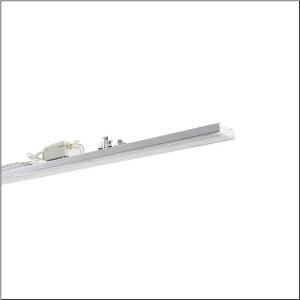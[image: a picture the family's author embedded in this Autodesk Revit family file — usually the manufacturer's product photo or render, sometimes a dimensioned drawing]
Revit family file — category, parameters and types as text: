
# Revit family: licross_r__21_recessed_ho_52te12dv4l2m3s4_36cd
name_source: partatom
category: Lighting Fixtures
units: mm (PartAtom-declared; Revit-internal decimal feet)

## family parameters
Cut with Voids When Loaded = No
Host = Face
Light Source = No
Part Type = Normal
Room Calculation Point = No
Round Connector Dimension = Use Diameter
Shared = No

## types (1)
- --- (1 x LED, 910 lm, 6.4 W, 4000K)
    Apparent Load = 6 VA
    CIE Flux Codes = 69 91 98 100 100
    Color Rendering = 80
    Color Temperature = 4000K
    Default Elevation = 1800 mm
    Description = Licross® 21 Recessed HO, luminaire insert, of sheet steel, galvanised, coil coated, white, length: 2.250mm, width: 66mm, height: 67mm, LED rated luminous flux: 22.710lm, light colour: 840, control gear: DALI 2, with plug, 6-pole, with phase selection, for trunking rail, 9 or 11-core, mains connection: 220..240V, AC, 50/60Hz, rated input power: 129W, for trunking rail, 9-/11-core, halogen-free wiring, for emergency light function, converter,control gear: single battery element, battery: LiFeP04, 9Ah, primary optical cover: cover, of PMMA, light emission: direct distribution, primary light characteristic: symmetric, protection rating (complete): IP54, insulation class (complete): insulation class I (protective earthing), certification: CE, UKCA, protection symbol: D if used in an environment with non-conductive dust loads with corresponding accessories, impact resistance: IK06, permissible ambient temperature for indoor applications: +5..+30°C, standard: EN 60598-2-22, LABS conformity tested according to VDMA 24364:2018-05, reducing of maximum allowable ambient temperature of 5°C with ceiling mounting, corresponds to IFS (International Featured Standards) requirements for safety and quality in the food industry, packaging unit: 1 piece
    Height = 58 mm
    Lamp = 1 x LED
    Lamp Light Flux = 910 lm
    Lamp Power = 6.4 W
    Lamp count = 1
    Length = 2250 mm
    Luminous efficacy = 142 lm/W
    Manufacturer = Siteco
    ModVariant = No
    Model = 52TE12DV4L2M3S4
    Mounting Place = Ceiling
    Mounting Type = Pendant
    Number of Poles = 1
    OnlyDefault = Yes
    Power Factor = 1
    Product Name = Licross® 21 Recessed HO
    Product group = luminaire insert
    ProductGroupID = 901
    Protection Class = Protection class I
    Protection Degree = IP 54
    RLX_Detail_Level = 1
    RLX_Emergency_Light_Flux = 0 lm
    RLX_Emergency_Type = 0
    RLX_Emergency_Type_DB = No
    RlxData = <blob elided: 30241 chars, md5=5925f3f0>
    Socket = socket
    Standby Power = 0 W
    System Light Flux = 910 lm
    System Power = 6 W
    Type Comments = : emergency light operation: 3 h
    Type Image = l_1296930.jpg
    URL = http://relux.com
    VarID = @adj_039453
    Voltage = 0 V
    Weight = 0.00 kg
    Width = 66 mm

## geometry (parser evidence)
native form markers: Blend x4, Sweep x10
no freeform markers — native parametric forms only
